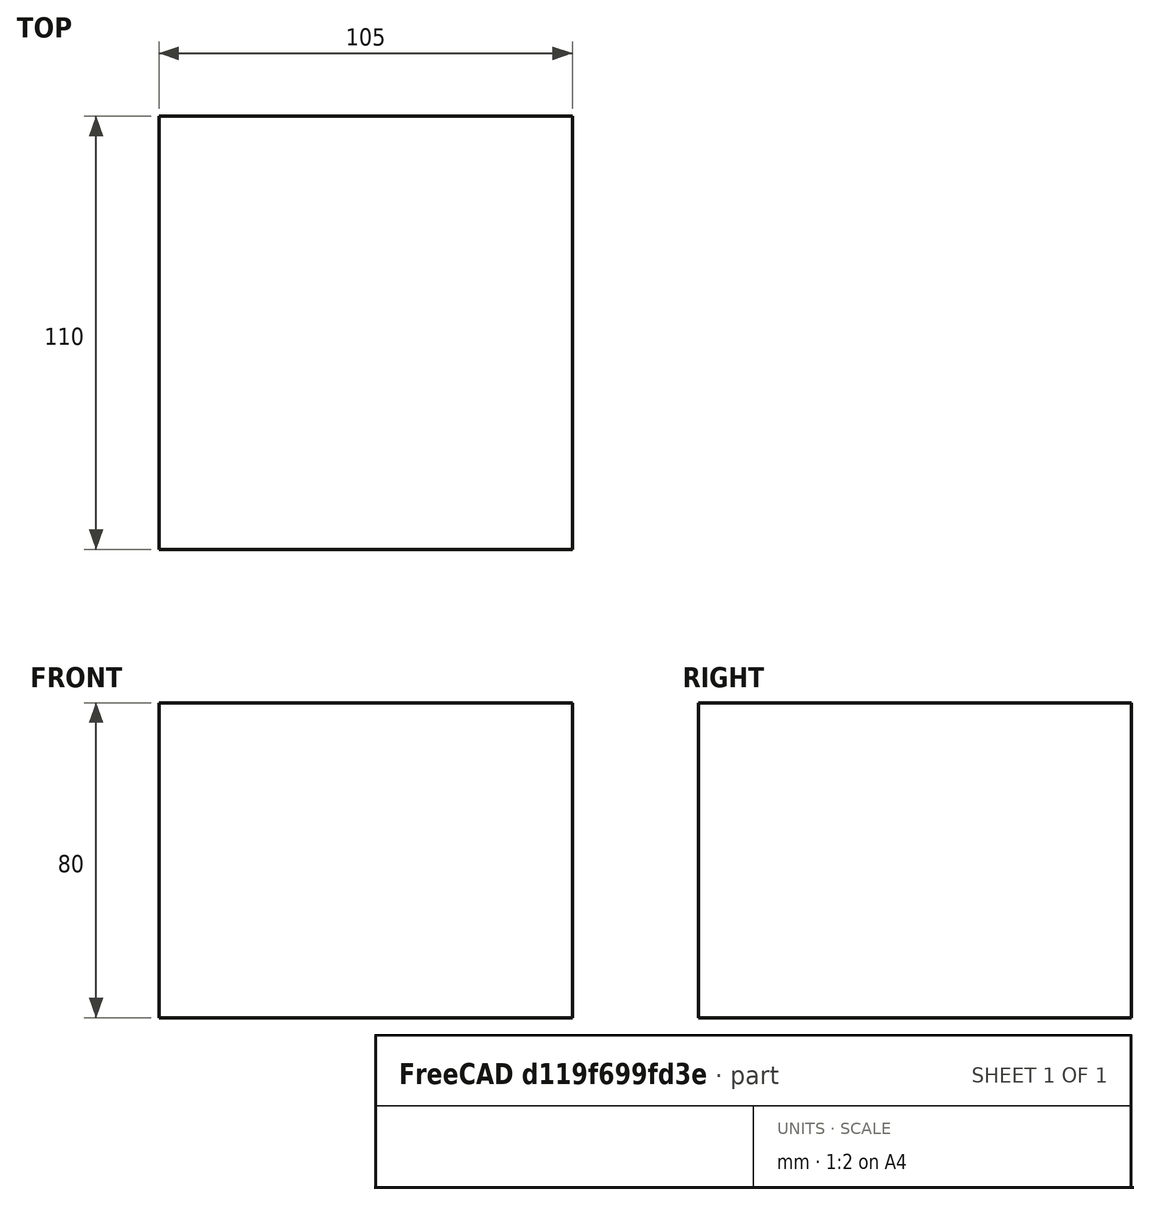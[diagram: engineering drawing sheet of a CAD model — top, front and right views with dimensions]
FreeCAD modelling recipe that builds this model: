
FCSTD DOCUMENT  (FreeCAD 0.15R4671 (Git))
Label: Halteplatte X-Achse
License: All rights reserved
LicenseURL: http://de.wikipedia.org/wiki/Alle_Rechte_vorbehalten
objects: Sketcher::SketchObject×2, PartDesign::Pad×1
note: 4 computed .brp shape members not serialized (recipe doc carries the construction recipe); baked Part::Feature solids carry a one-line shape summary decoded from their .brp

FEATURE [Sketcher::SketchObject] Sketch
  Placement = pos=(0,0,0) rot=(-1,0,0;4.71239rad)
  sketch-geometry (4):
    g0: LineSegment StartX=-52.5 StartY=40 StartZ=0 EndX=52.5 EndY=40 EndZ=0
    g1: LineSegment StartX=52.5 StartY=40 StartZ=0 EndX=52.5 EndY=-40 EndZ=0
    g2: LineSegment StartX=52.5 StartY=-40 StartZ=0 EndX=-52.5 EndY=-40 EndZ=0
    g3: LineSegment StartX=-52.5 StartY=-40 StartZ=0 EndX=-52.5 EndY=40 EndZ=0
  constraints (12):
    c: Coincident(g0,g1)
    c: Coincident(g1,g2)
    c: Coincident(g2,g3)
    c: Coincident(g3,g0)
    c: Horizontal(g0)
    c: Horizontal(g2)
    c: Vertical(g1)
    c: Vertical(g3)
    c: Symmetric(g2,g1,g-2)
    c: Symmetric(g1,g0,g-1)
    c: DistanceX(g2) = -105
    c: DistanceY(g1) = -80
FEATURE [PartDesign::Pad] Pad
  Length = 110
  Length2 = 100
  Midplane = true
  Placement = pos=(0,0,0) rot=(-1,0,0;4.71239rad)
  Sketch = -> Sketch
  Type = 0
FEATURE [Sketcher::SketchObject] Sketch001
  Placement = pos=(0,-55,0) rot=(1,0,0;1.5708rad)
  Support = -> Pad [Face6]
  sketch-geometry (2):
    g0: Circle CenterX=-44.3366 CenterY=0 CenterZ=0 NormalX=0 NormalY=0 NormalZ=1 Radius=2.1
    g1: Circle CenterX=44.3366 CenterY=0 CenterZ=0 NormalX=0 NormalY=0 NormalZ=1 Radius=2.1
  constraints (5):
    c: PointOnObject(g0,g-1)
    c: Symmetric(g1,g0,g-2)
    c: Equal(g0,g1)
    c: Radius(g1) = 2.1
    c: DistanceX(g0,g1) = 88.6731
